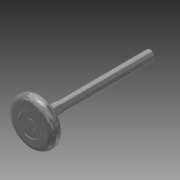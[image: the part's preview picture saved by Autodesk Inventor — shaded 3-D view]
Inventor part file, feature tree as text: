
AUTODESK INVENTOR PART (.ipt)
format: ipt  version: 2015 SP1 (Build 190203100, 203)  size: 150,016 bytes
history: native  units: in
note: dims shown in document units (in); Inventor stores cm internally (conversion verified against a paired STEP export)
features: extrude x5, sketch x5, fillet x1, plane x1, projected_geometry x1
ambient origin geometry x8: Origin, YZ Plane, XZ Plane, XY Plane, X Axis, Y Axis, Z Axis, Center Point
bodies: Solid1 (feature_tree)
feature tree (13):
  extrude  "Extrusion1"  Depth=0.5in
  fillet  "Fillet1"  Radius=0.5in
  extrude  "Extrusion2"  Depth=0.25in
  plane  "Work Plane1"
  extrude  "Extrusion3"  Depth=5.25in
  extrude  "Extrusion4"  Depth=0.475in TaperAngle=0.0deg
  extrude  "Extrusion5"  Depth=0.125in TaperAngle=0.0deg
  sketch  "Sketch1"  dims[d0=2.0in d1=1.0in d2=0.5in d3=0.0in]
  sketch  "Sketch2"  dims[d4=0.25in d5=0.4375in]
  projected_geometry  "Projected Loop1"
  sketch  "Sketch3"  dims[d6=5.25in d7=0.0in d8=0.975in]
  sketch  "Sketch4"  dims[d9=0.453in d10=0.475in d11=0.0in]
  sketch  "Sketch5"  dims[d12=0.5in d13=1.0in d14=0.0in d15=1.5in d16=0.125in d17=0.0in]
